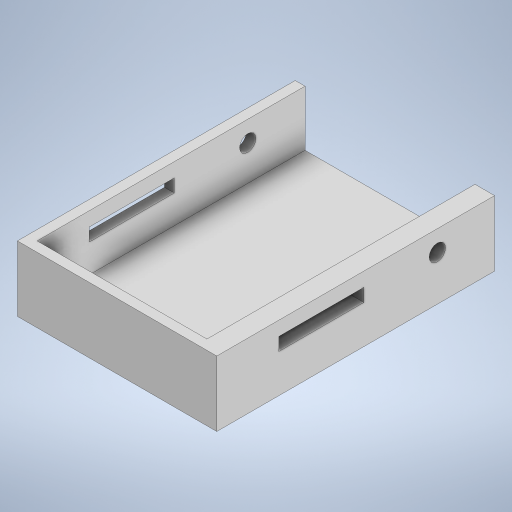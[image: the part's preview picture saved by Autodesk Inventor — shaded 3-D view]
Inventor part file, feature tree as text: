
AUTODESK INVENTOR PART (.ipt)
format: ipt  version: 2023 (Build 270158000, 158)  size: 257,536 bytes
history: native  units: in
note: dims shown in document units (in); Inventor stores cm internally (conversion verified against a paired STEP export)
features: sketch x6, extrude x5, shell x1
ambient origin geometry x8: Origin, YZ Plane, XZ Plane, XY Plane, X Axis, Y Axis, Z Axis, Center Point
bodies: Solid1 (feature_tree)
feature tree (12):
  extrude  "Extrusion1"  Depth=3.3465in
  shell  "Shell1"  Thickness=0.7874in
  sketch  "Sketch4"  dims[d4=0.1181in d17=0.3937in d18=0.0in]
  extrude  "Extrusion3"  Depth=0.3937in TaperAngle=0.0deg
  sketch  "Sketch6"  dims[d22=0.4606in d25=0.1181in d26=0.0in]
  extrude  "Extrusion5"  Depth=0.1575in
  extrude  "Extrusion6"  Depth=0.1181in TaperAngle=0.0deg
  extrude  "Extrusion8"  Depth=1.7717in
  sketch  "Sketch2"  dims[d0=2.2835in d1=3.3465in d2=0.7874in d3=0.0in]
  sketch  "Sketch5"  dims[d19=1.0236in d20=0.1575in]
  sketch  "Sketch7"  dims[d27=0.0in d28=0.0in d32=1.7717in]
  sketch  "Sketch9"  dims[d33=0.1969in d34=0.0in d35=0.0in d13=0.0197in d14=0.0344in d15=0.0197in d16=0.0344in]
